# Revit family: Amalphi Basin 50cm PP
name_source: partatom
category: Plumbing Fixtures
units: mm (PartAtom-declared; Revit-internal decimal feet)

## family parameters
Always vertical = Yes
Cut with Voids When Loaded = No
Enable Cutting in Views = No
Host = Wall
Maintain Annotation Orientation = No
OmniClass Number = 23.45.00.00
OmniClass Title = Sanitary, Laundry, and Cleaning Equipment
Part Type = Normal
Room Calculation Point = No
Round Connector Dimension = Use Diameter
Shared = No

## types (3) — shared parameters
Category = Basins – Wall Hung
Ceramic = Ceramic
Colour = White
Fixing Details = Basin Fixing Bolts not supplied, 8mm to 10mm bolts recommended
Manufacturer = Lecico SA
Material = Vitreous China
Silver = Silver
URL = https://www.lecicosa.co.za
zero-valued in all types: Default Elevation

## per-type parameters (varying)
| type | Full Pedestal | Half pedestal | Model | No pedestal | Product code | Technical Dimensions |
| Amalphi Basin 50cm PP | No | No | Amalphi Basin 50cm PP - no pedestal | Yes | AMPBASWHU0500BE | W502 x H182 x D410mm |
| Amalphi Basin 50cm PP - with full pedestal | Yes | No | Amalphi Basin 50cm PP - with full pedestal | No | AMPDUOBAS0500BE | W502 x H821 x D410mm |
| Amalphi Basin 50cm PP - with half pedestal | No | Yes | Amalphi Basin 50cm PP - with half pedestal | Yes | AMPBASWHU0500BE, MADPEDSEM0000UE | W502 x H182 x D410mm |

## geometry (parser evidence)
native form markers: Sweep x8
no freeform markers — native parametric forms only
